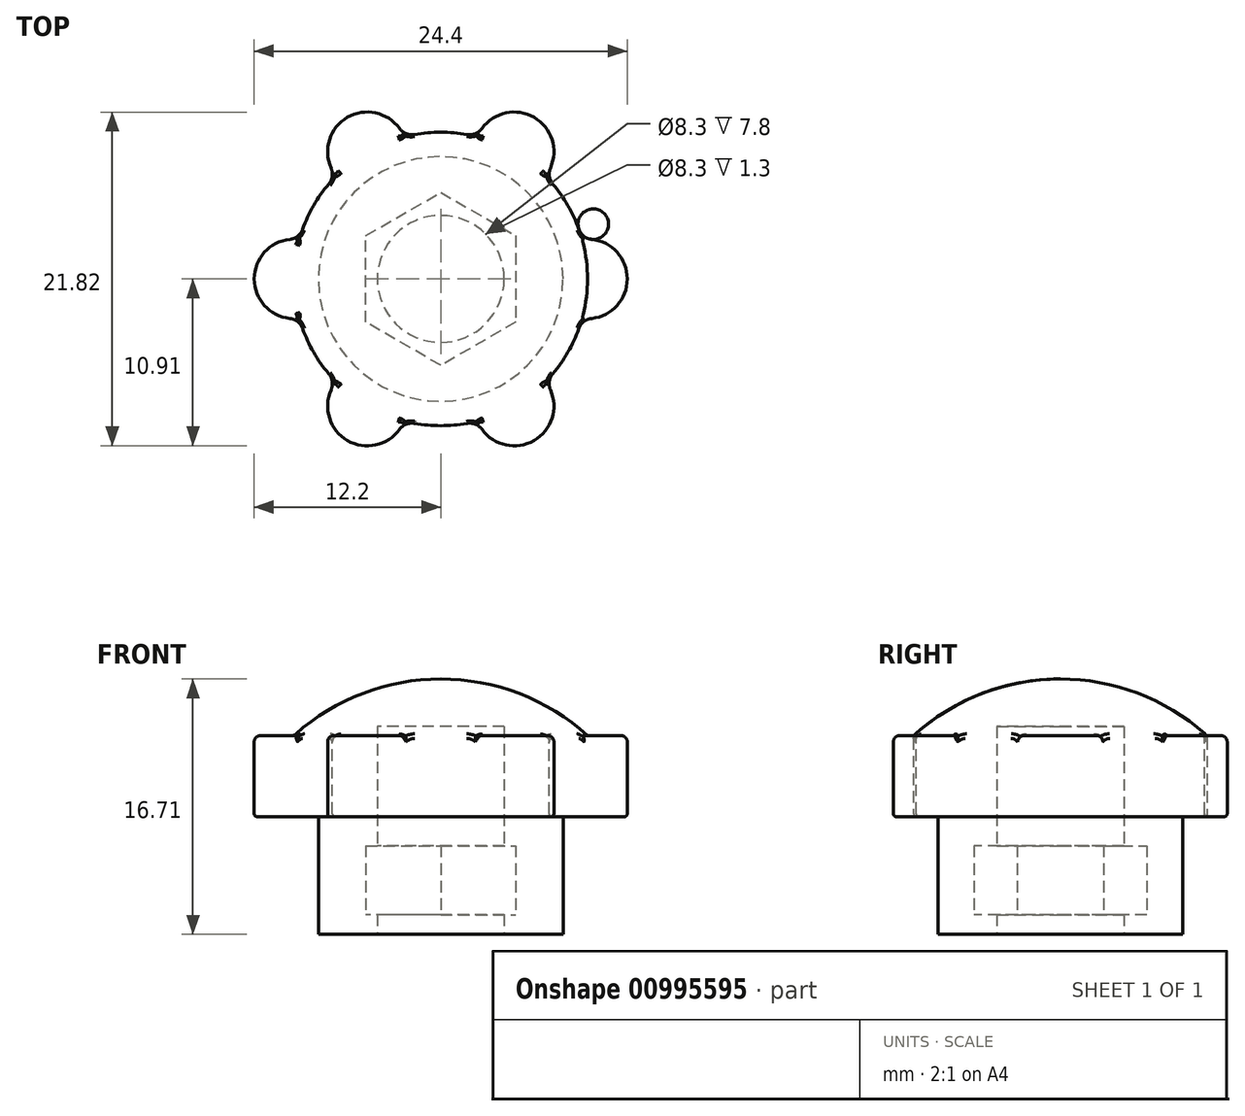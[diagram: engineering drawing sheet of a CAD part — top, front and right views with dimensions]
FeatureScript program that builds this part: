
annotation { "Feature Type Name" : "Feature", "Feature Type Description" : "" }
export const myFeature = defineFeature(function(context is Context, id is Id, definition is map)
    precondition{}
    {
        {
            var Q0;
            Q0=qCreatedBy(makeId("Top.planeOp"),FACE);
            var sketch = newSketch(context, id + "F0", { "sketchPlane" : qUnion([Q0])});
            skCircle(sketch, "E0", {"center": v(0, 0) * mm, "radius": 8 * mm});
            skCircle(sketch, "E1.cCircle", {"center": v(0, 0) * mm, "radius": 4.9 * mm, "construction": true});
            skLineSegment(sketch, "E1.0", {"start": v(4.9, 2.83) * mm, "end": v(4.9, -2.83) * mm});
            skLineSegment(sketch, "E1.1", {"start": v(4.9, -2.83) * mm, "end": v(0, -5.66) * mm});
            skLineSegment(sketch, "E1.2", {"start": v(0, -5.66) * mm, "end": v(-4.9, -2.83) * mm});
            skLineSegment(sketch, "E1.3", {"start": v(-4.9, -2.83) * mm, "end": v(-4.9, 2.83) * mm});
            skLineSegment(sketch, "E1.4", {"start": v(-4.9, 2.83) * mm, "end": v(0, 5.66) * mm});
            skLineSegment(sketch, "E1.5", {"start": v(0, 5.66) * mm, "end": v(4.9, 2.83) * mm});
            skPoint(sketch, "E1.0.midPoint", {"position": v(4.9, 0) * mm});
            skCircle(sketch, "E2", {"center": v(0, 0) * mm, "radius": 4.15 * mm});
            skSolve(sketch);
        }
        {
            var Q0;
            Q0=makeQuery(id+"F0.imprint","IMPRINT",FACE,{"disambiguationData":[TD([[makeQuery(id+"F0.imprint","IMPRINT",EDGE,{"derivedFrom":sQuery(id+"F0.wireOp",EDGE,"E0")}),1.0]])]});
            var Q1;
            Q1=makeQuery(id+"F0.imprint","IMPRINT",FACE,{"disambiguationData":[TD([[makeQuery(id+"F0.imprint","IMPRINT",EDGE,{"derivedFrom":sQuery(id+"F0.wireOp",EDGE,"E1.0")}),-1.0]])]});
            extrude(context, id + "F1", {"entities" : qUnion([Q0, Q1]), "depth" : 1.3 * mm, "offsetDistance" : 25 * mm});
        }
        {
            var Q0;
            Q0=makeQuery(id+"F0.imprint","IMPRINT",FACE,{"disambiguationData":[TD([[makeQuery(id+"F0.imprint","IMPRINT",EDGE,{"derivedFrom":sQuery(id+"F0.wireOp",EDGE,"E0")}),1.0]])]});
            extrude(context, id + "F2", {"entities" : qUnion([Q0]), "operationType" : NewBodyOperationType.ADD, "depth" : (4.5 + 1.3) * mm, "offsetDistance" : 25 * mm});
        }
        {
            var Q0;
            Q0=makeQuery(id+"F0.imprint","IMPRINT",FACE,{"disambiguationData":[TD([[makeQuery(id+"F0.imprint","IMPRINT",EDGE,{"derivedFrom":sQuery(id+"F0.wireOp",EDGE,"E0")}),1.0]])]});
            var Q1;
            Q1=makeQuery(id+"F0.imprint","IMPRINT",FACE,{"disambiguationData":[TD([[makeQuery(id+"F0.imprint","IMPRINT",EDGE,{"derivedFrom":sQuery(id+"F0.wireOp",EDGE,"E1.0")}),-1.0]])]});
            extrude(context, id + "F3", {"entities" : qUnion([Q0, Q1]), "operationType" : NewBodyOperationType.ADD, "depth" : 13.6 * mm, "offsetDistance" : 25 * mm, "hasSecondDirection" : true, "secondDirectionOppositeDirection" : false, "secondDirectionDepth" : 5.8 * mm});
        }
        {
            var Q0;
            Q0=qCreatedBy(makeId("Top.planeOp"),FACE);
            var sketch = newSketch(context, id + "F4", { "sketchPlane" : qUnion([Q0])});
            skCircle(sketch, "E3", {"center": v(0, 0) * mm, "radius": 9.6 * mm});
            skCircle(sketch, "E4", {"center": v(-9.6, 0) * mm, "radius": 2.6 * mm});
            skCircle(sketch, "E5.1.0", {"center": v(-4.8, 8.31) * mm, "radius": 2.6 * mm});
            skCircle(sketch, "E5.2.0", {"center": v(4.8, 8.31) * mm, "radius": 2.6 * mm});
            skCircle(sketch, "E5.3.0", {"center": v(9.6, 0) * mm, "radius": 2.6 * mm});
            skCircle(sketch, "E5.4.0", {"center": v(4.8, -8.31) * mm, "radius": 2.6 * mm});
            skCircle(sketch, "E5.5.0", {"center": v(-4.8, -8.31) * mm, "radius": 2.6 * mm});
            skLineSegment(sketch, "E5.anchor1", {"start": v(0, 0) * mm, "end": v(-9.6, 0) * mm, "construction": true});
            skLineSegment(sketch, "E5.anchor2", {"start": v(0, 0) * mm, "end": v(-4.8, -8.31) * mm, "construction": true});
            skCircle(sketch, "E6", {"center": v(0, 0) * mm, "radius": 4.15 * mm});
            skSolve(sketch);
        }
        {
            var Q0;
            {var subQ1=sQuery(id+"F4.wireOp",EDGE,"E3");var subQ9=sQuery(id+"F4.wireOp",EDGE,"E5.2.0");var subQ10=makeQuery(id+"F4.imprint","INTERSECT",VERTEX,{"disambiguationData":[OD(0.0)],"derivedFrom":[subQ1,subQ9]});Q0=makeQuery(id+"F4.imprint","IMPRINT",FACE,{"disambiguationData":[TD([[makeQuery(id+"F4.imprint","IMPRINT",EDGE,{"disambiguationData":[TD([[subQ10,1.0]])],"derivedFrom":subQ1}),1.0]])]});}
            var Q1;
            {var subQ0=sQuery(id+"F4.wireOp",EDGE,"E5.1.0");var subQ1=sQuery(id+"F4.wireOp",EDGE,"E3");var subQ2=makeQuery(id+"F4.imprint","INTERSECT",VERTEX,{"disambiguationData":[OD(0.0)],"derivedFrom":[subQ1,subQ0]});Q1=makeQuery(id+"F4.imprint","IMPRINT",FACE,{"disambiguationData":[TD([[makeQuery(id+"F4.imprint","IMPRINT",EDGE,{"disambiguationData":[TD([[subQ2,-1.0]])],"derivedFrom":subQ1}),-1.0]])]});}
            var Q2;
            {var subQ0=sQuery(id+"F4.wireOp",EDGE,"E4");var subQ1=sQuery(id+"F4.wireOp",EDGE,"E3");var subQ2=makeQuery(id+"F4.imprint","INTERSECT",VERTEX,{"disambiguationData":[OD(0.0)],"derivedFrom":[subQ1,subQ0]});Q2=makeQuery(id+"F4.imprint","IMPRINT",FACE,{"disambiguationData":[TD([[makeQuery(id+"F4.imprint","IMPRINT",EDGE,{"disambiguationData":[TD([[subQ2,-1.0]])],"derivedFrom":subQ1}),-1.0]])]});}
            var Q3;
            {var subQ0=sQuery(id+"F4.wireOp",EDGE,"E5.5.0");var subQ1=sQuery(id+"F4.wireOp",EDGE,"E3");var subQ2=makeQuery(id+"F4.imprint","INTERSECT",VERTEX,{"disambiguationData":[OD(0.0)],"derivedFrom":[subQ1,subQ0]});Q3=makeQuery(id+"F4.imprint","IMPRINT",FACE,{"disambiguationData":[TD([[makeQuery(id+"F4.imprint","IMPRINT",EDGE,{"disambiguationData":[TD([[subQ2,-1.0]])],"derivedFrom":subQ1}),-1.0]])]});}
            var Q4;
            {var subQ0=sQuery(id+"F4.wireOp",EDGE,"E5.4.0");var subQ1=sQuery(id+"F4.wireOp",EDGE,"E3");var subQ2=makeQuery(id+"F4.imprint","INTERSECT",VERTEX,{"disambiguationData":[OD(0.0)],"derivedFrom":[subQ1,subQ0]});Q4=makeQuery(id+"F4.imprint","IMPRINT",FACE,{"disambiguationData":[TD([[makeQuery(id+"F4.imprint","IMPRINT",EDGE,{"disambiguationData":[TD([[subQ2,-1.0]])],"derivedFrom":subQ1}),-1.0]])]});}
            var Q5;
            {var subQ0=sQuery(id+"F4.wireOp",EDGE,"E5.3.0");var subQ1=sQuery(id+"F4.wireOp",EDGE,"E3");var subQ2=makeQuery(id+"F4.imprint","INTERSECT",VERTEX,{"disambiguationData":[OD(0.0)],"derivedFrom":[subQ1,subQ0]});Q5=makeQuery(id+"F4.imprint","IMPRINT",FACE,{"disambiguationData":[TD([[makeQuery(id+"F4.imprint","IMPRINT",EDGE,{"disambiguationData":[TD([[subQ2,1.0]])],"derivedFrom":subQ1}),-1.0]])]});}
            var Q6;
            {var subQ0=sQuery(id+"F4.wireOp",EDGE,"E5.2.0");var subQ1=sQuery(id+"F4.wireOp",EDGE,"E3");var subQ2=makeQuery(id+"F4.imprint","INTERSECT",VERTEX,{"disambiguationData":[OD(0.0)],"derivedFrom":[subQ1,subQ0]});Q6=makeQuery(id+"F4.imprint","IMPRINT",FACE,{"disambiguationData":[TD([[makeQuery(id+"F4.imprint","IMPRINT",EDGE,{"disambiguationData":[TD([[subQ2,-1.0]])],"derivedFrom":subQ1}),-1.0]])]});}
            var Q7;
            {var subQ0=sQuery(id+"F4.wireOp",EDGE,"E5.1.0");var subQ1=sQuery(id+"F4.wireOp",EDGE,"E3");var subQ2=makeQuery(id+"F4.imprint","INTERSECT",VERTEX,{"disambiguationData":[OD(0.0)],"derivedFrom":[subQ1,subQ0]});Q7=makeQuery(id+"F4.imprint","IMPRINT",FACE,{"disambiguationData":[TD([[makeQuery(id+"F4.imprint","IMPRINT",EDGE,{"disambiguationData":[TD([[subQ2,-1.0]])],"derivedFrom":subQ1}),1.0]])]});}
            var Q8;
            {var subQ0=sQuery(id+"F4.wireOp",EDGE,"E4");var subQ1=sQuery(id+"F4.wireOp",EDGE,"E3");var subQ2=makeQuery(id+"F4.imprint","INTERSECT",VERTEX,{"disambiguationData":[OD(0.0)],"derivedFrom":[subQ1,subQ0]});Q8=makeQuery(id+"F4.imprint","IMPRINT",FACE,{"disambiguationData":[TD([[makeQuery(id+"F4.imprint","IMPRINT",EDGE,{"disambiguationData":[TD([[subQ2,-1.0]])],"derivedFrom":subQ1}),1.0]])]});}
            var Q9;
            {var subQ0=sQuery(id+"F4.wireOp",EDGE,"E5.5.0");var subQ1=sQuery(id+"F4.wireOp",EDGE,"E3");var subQ2=makeQuery(id+"F4.imprint","INTERSECT",VERTEX,{"disambiguationData":[OD(0.0)],"derivedFrom":[subQ1,subQ0]});Q9=makeQuery(id+"F4.imprint","IMPRINT",FACE,{"disambiguationData":[TD([[makeQuery(id+"F4.imprint","IMPRINT",EDGE,{"disambiguationData":[TD([[subQ2,-1.0]])],"derivedFrom":subQ1}),1.0]])]});}
            var Q10;
            {var subQ0=sQuery(id+"F4.wireOp",EDGE,"E5.4.0");var subQ1=sQuery(id+"F4.wireOp",EDGE,"E3");var subQ2=makeQuery(id+"F4.imprint","INTERSECT",VERTEX,{"disambiguationData":[OD(0.0)],"derivedFrom":[subQ1,subQ0]});Q10=makeQuery(id+"F4.imprint","IMPRINT",FACE,{"disambiguationData":[TD([[makeQuery(id+"F4.imprint","IMPRINT",EDGE,{"disambiguationData":[TD([[subQ2,-1.0]])],"derivedFrom":subQ1}),1.0]])]});}
            var Q11;
            {var subQ0=sQuery(id+"F4.wireOp",EDGE,"E5.3.0");var subQ1=sQuery(id+"F4.wireOp",EDGE,"E3");var subQ2=makeQuery(id+"F4.imprint","INTERSECT",VERTEX,{"disambiguationData":[OD(0.0)],"derivedFrom":[subQ1,subQ0]});Q11=makeQuery(id+"F4.imprint","IMPRINT",FACE,{"disambiguationData":[TD([[makeQuery(id+"F4.imprint","IMPRINT",EDGE,{"disambiguationData":[TD([[subQ2,1.0]])],"derivedFrom":subQ1}),1.0]])]});}
            var Q12;
            {var subQ0=sQuery(id+"F4.wireOp",EDGE,"E5.2.0");var subQ1=sQuery(id+"F4.wireOp",EDGE,"E3");var subQ2=makeQuery(id+"F4.imprint","INTERSECT",VERTEX,{"disambiguationData":[OD(0.0)],"derivedFrom":[subQ1,subQ0]});Q12=makeQuery(id+"F4.imprint","IMPRINT",FACE,{"disambiguationData":[TD([[makeQuery(id+"F4.imprint","IMPRINT",EDGE,{"disambiguationData":[TD([[subQ2,-1.0]])],"derivedFrom":subQ1}),1.0]])]});}
            extrude(context, id + "F5", {"entities" : qUnion([Q0, Q1, Q2, Q3, Q4, Q5, Q6, Q7, Q8, Q9, Q10, Q11, Q12]), "depth" : 13 * mm, "offsetDistance" : 25 * mm, "hasSecondDirection" : true, "secondDirectionOppositeDirection" : false, "secondDirectionDepth" : 7.7 * mm});
        }
        {
            var Q0;
            Q0=qCreatedBy(makeId("Right.planeOp"),FACE);
            var sketch = newSketch(context, id + "F6", { "sketchPlane" : qUnion([Q0])});
            skLineSegment(sketch, "E7", {"start": v(9.6, 13) * mm, "end": v(-9.6, 13) * mm});
            skLineSegment(sketch, "E8", {"start": v(0, 12.9) * mm, "end": v(0, 16.7) * mm});
            skArc(sketch, "E9", {"start": v(9.6, 13) * mm, "mid": v(0, 16.7) * mm, "end": v(-9.6, 13) * mm});
            skSolve(sketch);
        }
        {
            var Q0;
            {var subQ3=sQuery(id+"F6.wireOp",EDGE,"E8");Q0=makeQuery(id+"F6.imprint","IMPRINT",FACE,{"disambiguationData":[TD([[makeQuery(id+"F6.imprint","IMPRINT",EDGE,{"derivedFrom":subQ3}),1.0]])]});}
            var Q1;
            Q1=sQuery(id+"F6.wireOp",EDGE,"E8");
            revolve(context, id + "F7", {"surfaceOperationType" : NewSurfaceOperationType.NEW, "entities" : qUnion([Q0]), "axis" : qUnion([Q1]), "revolveType" : RevolveType.FULL});
        }
        {
            var Q0;
            Q0=makeQuery(id+"F0.imprint","IMPRINT",FACE,{"disambiguationData":[TD([[makeQuery(id+"F0.imprint","IMPRINT",EDGE,{"derivedFrom":sQuery(id+"F0.wireOp",EDGE,"E2")}),1.0]])]});
            extrude(context, id + "F8", {"entities" : qUnion([Q0]), "operationType" : NewBodyOperationType.REMOVE, "depth" : 13.6 * mm, "offsetDistance" : 25 * mm});
        }
        {
            var Q0;
            Q0=makeQuery(id+"F7.opRevolve","SWEPT_BODY",BODY,{"disambiguationData":[OSD([sQuery(id+"F6.wireOp",EDGE,"E7"),sQuery(id+"F6.wireOp",EDGE,"E8"),sQuery(id+"F6.wireOp",EDGE,"txRQOt1j-K5Gy-4ET2-xuzk-dy7WdRMizSXB")])]});
            var Q1;
            Q1=makeQuery(id+"F5.opExtrude","SWEPT_BODY",BODY,{"disambiguationData":[OSD([sQuery(id+"F4.wireOp",EDGE,"E3"),sQuery(id+"F4.wireOp",EDGE,"E4"),sQuery(id+"F4.wireOp",EDGE,"E5.1.0"),sQuery(id+"F4.wireOp",EDGE,"E5.2.0"),sQuery(id+"F4.wireOp",EDGE,"E5.3.0"),sQuery(id+"F4.wireOp",EDGE,"E5.4.0"),sQuery(id+"F4.wireOp",EDGE,"E5.5.0"),sQuery(id+"F4.wireOp",EDGE,"E6")])]});
            var Q2;
            Q2=makeQuery(id+"F1.opExtrude","SWEPT_BODY",BODY,{"disambiguationData":[OSD([sQuery(id+"F0.wireOp",EDGE,"E0"),sQuery(id+"F0.wireOp",EDGE,"E2")])]});
            booleanBodies(context, id + "F9", {"operationType" : BooleanOperationType.UNION, "tools" : qUnion([Q0, Q1, Q2])});
        }
        {
            var Q0;
            {var subQ0=sQuery(id+"F4.wireOp",EDGE,"E5.2.0");var subQ1=sQuery(id+"F4.wireOp",EDGE,"E3");Q0=makeQuery(id+"F5.opExtrude","SWEPT_EDGE",EDGE,{"disambiguationData":[OSD([subQ1,subQ0]),TDD([makeQuery(id+"F4.imprint","INTERSECT",VERTEX,{"disambiguationData":[OD(1.0)],"derivedFrom":[subQ1,subQ0]})])]});}
            var Q1;
            {var subQ0=sQuery(id+"F4.wireOp",EDGE,"E5.1.0");var subQ1=sQuery(id+"F4.wireOp",EDGE,"E3");Q1=makeQuery(id+"F5.opExtrude","SWEPT_EDGE",EDGE,{"disambiguationData":[OSD([subQ1,subQ0]),TDD([makeQuery(id+"F4.imprint","INTERSECT",VERTEX,{"disambiguationData":[OD(0.0)],"derivedFrom":[subQ1,subQ0]})])]});}
            var Q2;
            {var subQ0=sQuery(id+"F4.wireOp",EDGE,"E5.1.0");var subQ1=sQuery(id+"F4.wireOp",EDGE,"E3");Q2=makeQuery(id+"F5.opExtrude","SWEPT_EDGE",EDGE,{"disambiguationData":[OSD([subQ1,subQ0]),TDD([makeQuery(id+"F4.imprint","INTERSECT",VERTEX,{"disambiguationData":[OD(1.0)],"derivedFrom":[subQ1,subQ0]})])]});}
            var Q3;
            {var subQ0=sQuery(id+"F4.wireOp",EDGE,"E4");var subQ1=sQuery(id+"F4.wireOp",EDGE,"E3");Q3=makeQuery(id+"F5.opExtrude","SWEPT_EDGE",EDGE,{"disambiguationData":[OSD([subQ1,subQ0]),TDD([makeQuery(id+"F4.imprint","INTERSECT",VERTEX,{"disambiguationData":[OD(0.0)],"derivedFrom":[subQ1,subQ0]})])]});}
            var Q4;
            {var subQ0=sQuery(id+"F4.wireOp",EDGE,"E4");var subQ1=sQuery(id+"F4.wireOp",EDGE,"E3");Q4=makeQuery(id+"F5.opExtrude","SWEPT_EDGE",EDGE,{"disambiguationData":[OSD([subQ1,subQ0]),TDD([makeQuery(id+"F4.imprint","INTERSECT",VERTEX,{"disambiguationData":[OD(1.0)],"derivedFrom":[subQ1,subQ0]})])]});}
            var Q5;
            {var subQ0=sQuery(id+"F4.wireOp",EDGE,"E5.5.0");var subQ1=sQuery(id+"F4.wireOp",EDGE,"E3");Q5=makeQuery(id+"F5.opExtrude","SWEPT_EDGE",EDGE,{"disambiguationData":[OSD([subQ1,subQ0]),TDD([makeQuery(id+"F4.imprint","INTERSECT",VERTEX,{"disambiguationData":[OD(0.0)],"derivedFrom":[subQ1,subQ0]})])]});}
            var Q6;
            {var subQ0=sQuery(id+"F4.wireOp",EDGE,"E5.5.0");var subQ1=sQuery(id+"F4.wireOp",EDGE,"E3");Q6=makeQuery(id+"F5.opExtrude","SWEPT_EDGE",EDGE,{"disambiguationData":[OSD([subQ1,subQ0]),TDD([makeQuery(id+"F4.imprint","INTERSECT",VERTEX,{"disambiguationData":[OD(1.0)],"derivedFrom":[subQ1,subQ0]})])]});}
            var Q7;
            {var subQ0=sQuery(id+"F4.wireOp",EDGE,"E5.4.0");var subQ1=sQuery(id+"F4.wireOp",EDGE,"E3");Q7=makeQuery(id+"F5.opExtrude","SWEPT_EDGE",EDGE,{"disambiguationData":[OSD([subQ1,subQ0]),TDD([makeQuery(id+"F4.imprint","INTERSECT",VERTEX,{"disambiguationData":[OD(0.0)],"derivedFrom":[subQ1,subQ0]})])]});}
            var Q8;
            {var subQ0=sQuery(id+"F4.wireOp",EDGE,"E5.4.0");var subQ1=sQuery(id+"F4.wireOp",EDGE,"E3");Q8=makeQuery(id+"F5.opExtrude","SWEPT_EDGE",EDGE,{"disambiguationData":[OSD([subQ1,subQ0]),TDD([makeQuery(id+"F4.imprint","INTERSECT",VERTEX,{"disambiguationData":[OD(1.0)],"derivedFrom":[subQ1,subQ0]})])]});}
            var Q9;
            {var subQ0=sQuery(id+"F4.wireOp",EDGE,"E5.3.0");var subQ1=sQuery(id+"F4.wireOp",EDGE,"E3");Q9=makeQuery(id+"F5.opExtrude","SWEPT_EDGE",EDGE,{"disambiguationData":[OSD([subQ1,subQ0]),TDD([makeQuery(id+"F4.imprint","INTERSECT",VERTEX,{"disambiguationData":[OD(1.0)],"derivedFrom":[subQ1,subQ0]})])]});}
            var Q10;
            {var subQ0=sQuery(id+"F4.wireOp",EDGE,"E5.3.0");var subQ1=sQuery(id+"F4.wireOp",EDGE,"E3");Q10=makeQuery(id+"F5.opExtrude","SWEPT_EDGE",EDGE,{"disambiguationData":[OSD([subQ1,subQ0]),TDD([makeQuery(id+"F4.imprint","INTERSECT",VERTEX,{"disambiguationData":[OD(0.0)],"derivedFrom":[subQ1,subQ0]})])]});}
            var Q11;
            {var subQ0=sQuery(id+"F4.wireOp",EDGE,"E5.2.0");var subQ1=sQuery(id+"F4.wireOp",EDGE,"E3");Q11=makeQuery(id+"F5.opExtrude","SWEPT_EDGE",EDGE,{"disambiguationData":[OSD([subQ1,subQ0]),TDD([makeQuery(id+"F4.imprint","INTERSECT",VERTEX,{"disambiguationData":[OD(0.0)],"derivedFrom":[subQ1,subQ0]})])]});}
            fillet(context, id + "F10", {"entities" : qUnion([Q0, Q1, Q2, Q3, Q4, Q5, Q6, Q7, Q8, Q9, Q10, Q11]), "radius" : 1 * mm, "tangentPropagation" : true, "allowEdgeOverflow" : false});
        }
        {
            var Q0;
            {var subQ0=sQuery(id+"F4.wireOp",EDGE,"E3");Q0=makeQuery(id+"F9.opBoolean","MERGE",EDGE,{"derivedFrom":[makeQuery(id+"F5.opExtrude","CAP_EDGE",EDGE,{"disambiguationData":[OSD([subQ0]),TDD([makeQuery(id+"F4.imprint","IMPRINT",EDGE,{"disambiguationData":[TD([[makeQuery(id+"F4.imprint","INTERSECT",VERTEX,{"disambiguationData":[OD(1.0)],"derivedFrom":[subQ0,sQuery(id+"F4.wireOp",EDGE,"E5.4.0")]}),-1.0]])],"derivedFrom":subQ0})])],"isStart":false}),makeQuery(id+"F7.opRevolve","SWEPT_EDGE",EDGE,{"disambiguationData":[OSD([sQuery(id+"F6.wireOp",EDGE,"E7"),sQuery(id+"F6.wireOp",EDGE,"E9")])]})]});}
            var Q1;
            Q1=makeQuery(id+"F5.opExtrude","CAP_EDGE",EDGE,{"disambiguationData":[OSD([sQuery(id+"F4.wireOp",EDGE,"E5.4.0")])],"isStart":false});
            var Q2;
            Q2=makeQuery(id+"F5.opExtrude","CAP_EDGE",EDGE,{"disambiguationData":[OSD([sQuery(id+"F4.wireOp",EDGE,"E5.3.0")])],"isStart":false});
            var Q3;
            {var subQ0=sQuery(id+"F4.wireOp",EDGE,"E3");Q3=makeQuery(id+"F9.opBoolean","MERGE",EDGE,{"derivedFrom":[makeQuery(id+"F5.opExtrude","CAP_EDGE",EDGE,{"disambiguationData":[OSD([subQ0]),TDD([makeQuery(id+"F4.imprint","IMPRINT",EDGE,{"disambiguationData":[TD([[makeQuery(id+"F4.imprint","INTERSECT",VERTEX,{"disambiguationData":[OD(1.0)],"derivedFrom":[subQ0,sQuery(id+"F4.wireOp",EDGE,"E5.5.0")]}),-1.0]])],"derivedFrom":subQ0})])],"isStart":false}),makeQuery(id+"F7.opRevolve","SWEPT_EDGE",EDGE,{"disambiguationData":[OSD([sQuery(id+"F6.wireOp",EDGE,"E7"),sQuery(id+"F6.wireOp",EDGE,"E9")])]})]});}
            var Q4;
            Q4=makeQuery(id+"F5.opExtrude","CAP_EDGE",EDGE,{"disambiguationData":[OSD([sQuery(id+"F4.wireOp",EDGE,"E5.5.0")])],"isStart":false});
            var Q5;
            {var subQ0=sQuery(id+"F4.wireOp",EDGE,"E5.1.0");var subQ1=sQuery(id+"F4.wireOp",EDGE,"E3");var subQ2=sQuery(id+"F4.wireOp",EDGE,"E4");var subQ3=makeQuery(id+"F4.imprint","INTERSECT",VERTEX,{"disambiguationData":[OD(1.0)],"derivedFrom":[subQ1,subQ2]});var subQ4=sQuery(id+"F4.wireOp",EDGE,"E5.5.0");Q5=makeQuery(id+"F10.opFillet","BLEND_EDGE",EDGE,{"blendedFrom":[makeQuery(id+"F5.opExtrude","SWEPT_EDGE",EDGE,{"disambiguationData":[OSD([subQ1,subQ2]),TDD([subQ3])]}),makeQuery(id+"F9.opBoolean","SPLIT",FACE,{"disambiguationData":[TD([makeQuery(id+"F5.opExtrude","SWEPT_FACE",FACE,{"disambiguationData":[OSD([subQ2])]})])],"derivedFrom":makeQuery(id+"F5.opExtrude","CAP_FACE",FACE,{"disambiguationData":[OSD([subQ1,subQ2,subQ0,sQuery(id+"F4.wireOp",EDGE,"E5.2.0"),sQuery(id+"F4.wireOp",EDGE,"E5.3.0"),sQuery(id+"F4.wireOp",EDGE,"E5.4.0"),subQ4,sQuery(id+"F4.wireOp",EDGE,"E6")])],"isStart":false})})],"blendedInto":[makeQuery(id+"F9.opBoolean","SPLIT",FACE,{"disambiguationData":[TD([makeQuery(id+"F5.opExtrude","SWEPT_FACE",FACE,{"disambiguationData":[OSD([subQ2])]})])],"derivedFrom":makeQuery(id+"F5.opExtrude","CAP_FACE",FACE,{"disambiguationData":[OSD([subQ1,subQ2,subQ0,sQuery(id+"F4.wireOp",EDGE,"E5.2.0"),sQuery(id+"F4.wireOp",EDGE,"E5.3.0"),sQuery(id+"F4.wireOp",EDGE,"E5.4.0"),subQ4,sQuery(id+"F4.wireOp",EDGE,"E6")])],"isStart":false})})]});}
            var Q6;
            {var subQ0=sQuery(id+"F4.wireOp",EDGE,"E3");Q6=makeQuery(id+"F9.opBoolean","MERGE",EDGE,{"derivedFrom":[makeQuery(id+"F5.opExtrude","CAP_EDGE",EDGE,{"disambiguationData":[OSD([subQ0]),TDD([makeQuery(id+"F4.imprint","IMPRINT",EDGE,{"disambiguationData":[TD([[makeQuery(id+"F4.imprint","INTERSECT",VERTEX,{"disambiguationData":[OD(1.0)],"derivedFrom":[subQ0,sQuery(id+"F4.wireOp",EDGE,"E4")]}),-1.0]])],"derivedFrom":subQ0})])],"isStart":false}),makeQuery(id+"F7.opRevolve","SWEPT_EDGE",EDGE,{"disambiguationData":[OSD([sQuery(id+"F6.wireOp",EDGE,"E7"),sQuery(id+"F6.wireOp",EDGE,"E9")])]})]});}
            var Q7;
            {var subQ0=sQuery(id+"F4.wireOp",EDGE,"E3");Q7=makeQuery(id+"F9.opBoolean","MERGE",EDGE,{"derivedFrom":[makeQuery(id+"F5.opExtrude","CAP_EDGE",EDGE,{"disambiguationData":[OSD([subQ0]),TDD([makeQuery(id+"F4.imprint","IMPRINT",EDGE,{"disambiguationData":[TD([[makeQuery(id+"F4.imprint","INTERSECT",VERTEX,{"disambiguationData":[OD(1.0)],"derivedFrom":[subQ0,sQuery(id+"F4.wireOp",EDGE,"E5.1.0")]}),-1.0]])],"derivedFrom":subQ0})])],"isStart":false}),makeQuery(id+"F7.opRevolve","SWEPT_EDGE",EDGE,{"disambiguationData":[OSD([sQuery(id+"F6.wireOp",EDGE,"E7"),sQuery(id+"F6.wireOp",EDGE,"E9")])]})]});}
            var Q8;
            Q8=makeQuery(id+"F5.opExtrude","CAP_EDGE",EDGE,{"disambiguationData":[OSD([sQuery(id+"F4.wireOp",EDGE,"E5.1.0")])],"isStart":false});
            var Q9;
            Q9=makeQuery(id+"F5.opExtrude","CAP_EDGE",EDGE,{"disambiguationData":[OSD([sQuery(id+"F4.wireOp",EDGE,"E5.2.0")])],"isStart":false});
            var Q10;
            {var subQ0=sQuery(id+"F4.wireOp",EDGE,"E3");Q10=makeQuery(id+"F9.opBoolean","MERGE",EDGE,{"derivedFrom":[makeQuery(id+"F5.opExtrude","CAP_EDGE",EDGE,{"disambiguationData":[OSD([subQ0]),TDD([makeQuery(id+"F4.imprint","IMPRINT",EDGE,{"disambiguationData":[TD([[makeQuery(id+"F4.imprint","INTERSECT",VERTEX,{"disambiguationData":[OD(1.0)],"derivedFrom":[subQ0,sQuery(id+"F4.wireOp",EDGE,"E5.2.0")]}),-1.0]])],"derivedFrom":subQ0})])],"isStart":false}),makeQuery(id+"F7.opRevolve","SWEPT_EDGE",EDGE,{"disambiguationData":[OSD([sQuery(id+"F6.wireOp",EDGE,"E7"),sQuery(id+"F6.wireOp",EDGE,"E9")])]})]});}
            var Q11;
            {var subQ0=sQuery(id+"F4.wireOp",EDGE,"E3");Q11=makeQuery(id+"F9.opBoolean","MERGE",EDGE,{"derivedFrom":[makeQuery(id+"F5.opExtrude","CAP_EDGE",EDGE,{"disambiguationData":[OSD([subQ0]),TDD([makeQuery(id+"F4.imprint","IMPRINT",EDGE,{"disambiguationData":[TD([[makeQuery(id+"F4.imprint","INTERSECT",VERTEX,{"disambiguationData":[OD(0.0)],"derivedFrom":[subQ0,sQuery(id+"F4.wireOp",EDGE,"E5.2.0")]}),1.0]])],"derivedFrom":subQ0})])],"isStart":false}),makeQuery(id+"F7.opRevolve","SWEPT_EDGE",EDGE,{"disambiguationData":[OSD([sQuery(id+"F6.wireOp",EDGE,"E7"),sQuery(id+"F6.wireOp",EDGE,"E9")])]})]});}
            fillet(context, id + "F11", {"entities" : qUnion([Q0, Q1, Q2, Q3, Q4, Q5, Q6, Q7, Q8, Q9, Q10, Q11]), "radius" : 0.4 * mm, "tangentPropagation" : true, "allowEdgeOverflow" : false});
        }
        {
            var Q0;
            {var subQ2=sQuery(id+"F4.wireOp",EDGE,"E5.4.0");var subQ4=sQuery(id+"F6.wireOp",EDGE,"E9");Q0=makeQuery(id+"F9.opBoolean","SPLIT",EDGE,{"disambiguationData":[TD([makeQuery(id+"F5.opExtrude","SWEPT_FACE",FACE,{"disambiguationData":[OSD([subQ2])]})])],"derivedFrom":makeQuery(id+"F7.opRevolve","SWEPT_EDGE",EDGE,{"disambiguationData":[OSD([sQuery(id+"F6.wireOp",EDGE,"E7"),subQ4])]})});}
            var Q1;
            {var subQ0=sQuery(id+"F4.wireOp",EDGE,"E5.5.0");var subQ4=sQuery(id+"F6.wireOp",EDGE,"E9");Q1=makeQuery(id+"F9.opBoolean","SPLIT",EDGE,{"disambiguationData":[TD([makeQuery(id+"F5.opExtrude","SWEPT_FACE",FACE,{"disambiguationData":[OSD([subQ0])]})])],"derivedFrom":makeQuery(id+"F7.opRevolve","SWEPT_EDGE",EDGE,{"disambiguationData":[OSD([sQuery(id+"F6.wireOp",EDGE,"E7"),subQ4])]})});}
            var Q2;
            {var subQ0=sQuery(id+"F4.wireOp",EDGE,"E4");var subQ4=sQuery(id+"F6.wireOp",EDGE,"E9");Q2=makeQuery(id+"F9.opBoolean","SPLIT",EDGE,{"disambiguationData":[TD([makeQuery(id+"F5.opExtrude","SWEPT_FACE",FACE,{"disambiguationData":[OSD([subQ0])]})])],"derivedFrom":makeQuery(id+"F7.opRevolve","SWEPT_EDGE",EDGE,{"disambiguationData":[OSD([sQuery(id+"F6.wireOp",EDGE,"E7"),subQ4])]})});}
            var Q3;
            {var subQ0=sQuery(id+"F4.wireOp",EDGE,"E5.1.0");var subQ4=sQuery(id+"F6.wireOp",EDGE,"E9");Q3=makeQuery(id+"F9.opBoolean","SPLIT",EDGE,{"disambiguationData":[TD([makeQuery(id+"F5.opExtrude","SWEPT_FACE",FACE,{"disambiguationData":[OSD([subQ0])]})])],"derivedFrom":makeQuery(id+"F7.opRevolve","SWEPT_EDGE",EDGE,{"disambiguationData":[OSD([sQuery(id+"F6.wireOp",EDGE,"E7"),subQ4])]})});}
            var Q4;
            {var subQ0=sQuery(id+"F4.wireOp",EDGE,"E5.2.0");var subQ4=sQuery(id+"F6.wireOp",EDGE,"E9");Q4=makeQuery(id+"F9.opBoolean","SPLIT",EDGE,{"disambiguationData":[TD([makeQuery(id+"F5.opExtrude","SWEPT_FACE",FACE,{"disambiguationData":[OSD([subQ0])]})])],"derivedFrom":makeQuery(id+"F7.opRevolve","SWEPT_EDGE",EDGE,{"disambiguationData":[OSD([sQuery(id+"F6.wireOp",EDGE,"E7"),subQ4])]})});}
            var Q5;
            {var subQ0=sQuery(id+"F4.wireOp",EDGE,"E5.3.0");var subQ4=sQuery(id+"F6.wireOp",EDGE,"E9");Q5=makeQuery(id+"F9.opBoolean","SPLIT",EDGE,{"disambiguationData":[TD([makeQuery(id+"F5.opExtrude","SWEPT_FACE",FACE,{"disambiguationData":[OSD([subQ0])]})])],"derivedFrom":makeQuery(id+"F7.opRevolve","SWEPT_EDGE",EDGE,{"disambiguationData":[OSD([sQuery(id+"F6.wireOp",EDGE,"E7"),subQ4])]})});}
            fillet(context, id + "F12", {"entities" : qUnion([Q0, Q1, Q2, Q3, Q4, Q5]), "radius" : 0.4 * mm, "tangentPropagation" : true, "allowEdgeOverflow" : false});
        }
        {
            var Q0;
            Q0=makeQuery(id+"F5.opExtrude","CAP_EDGE",EDGE,{"disambiguationData":[OSD([sQuery(id+"F4.wireOp",EDGE,"E4")])],"isStart":true});
            fillet(context, id + "F13", {"entities" : qUnion([Q0]), "radius" : 0.2 * mm, "tangentPropagation" : true, "allowEdgeOverflow" : false});
        }
    });
